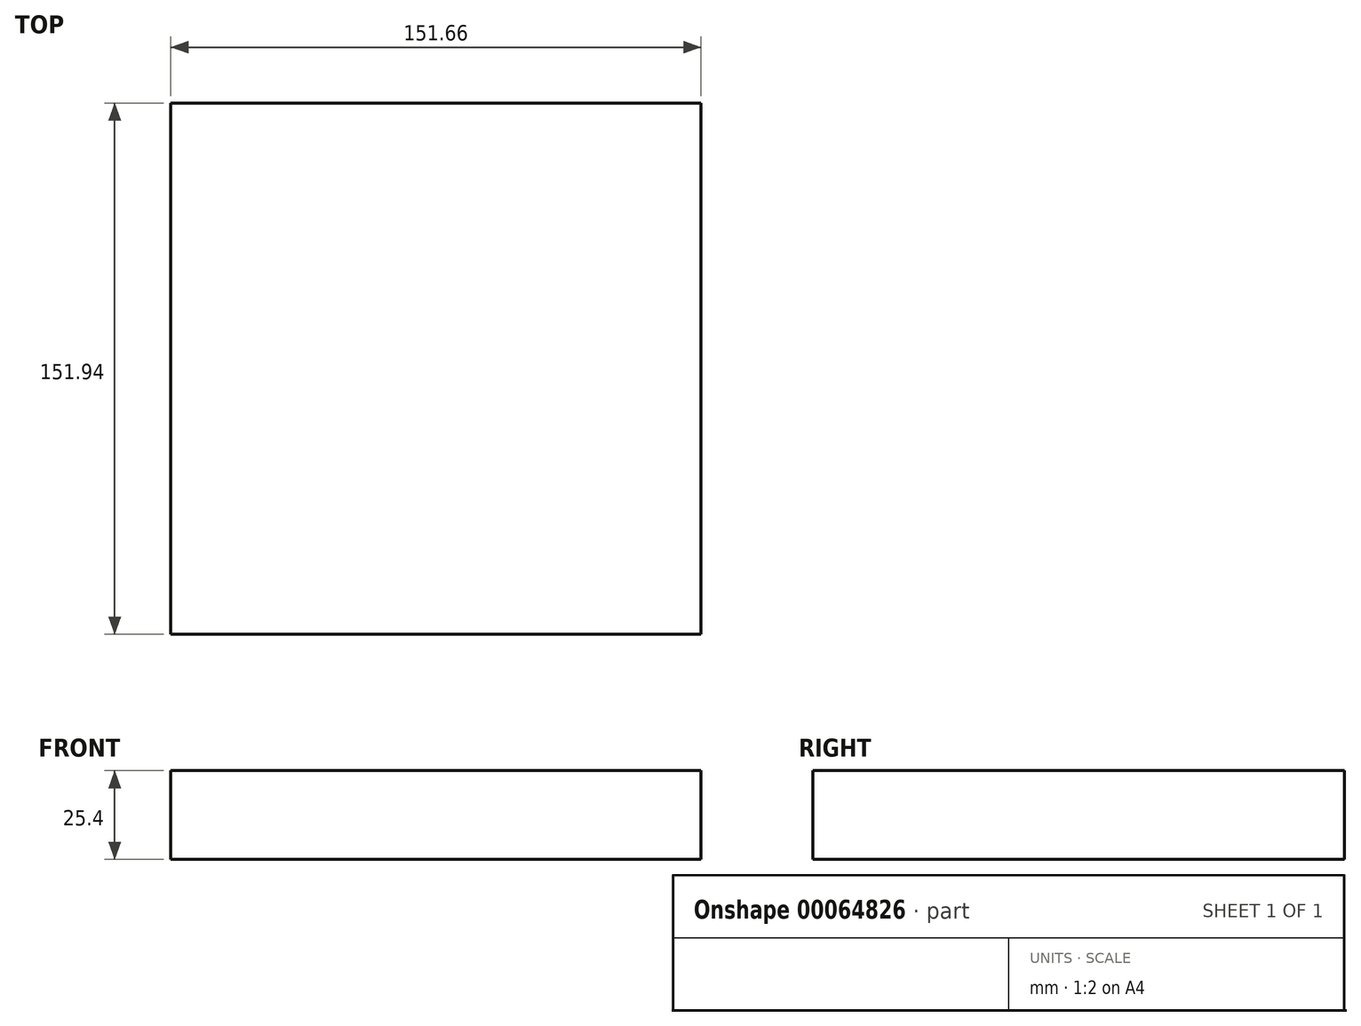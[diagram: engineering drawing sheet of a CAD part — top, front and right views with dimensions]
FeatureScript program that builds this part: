
annotation { "Feature Type Name" : "Feature", "Feature Type Description" : "" }
export const myFeature = defineFeature(function(context is Context, id is Id, definition is map)
    precondition{}
    {
        {
            var Q0;
            Q0=qCreatedBy(makeId("Top.planeOp"),FACE);
            var sketch = newSketch(context, id + "F0", { "sketchPlane" : qUnion([Q0])});
            skLineSegment(sketch, "E0.bottom", {"start": v(-75.74, -76.22) * mm, "end": v(75.92, -76.22) * mm});
            skLineSegment(sketch, "E0.top", {"start": v(-75.74, 75.72) * mm, "end": v(75.92, 75.72) * mm});
            skLineSegment(sketch, "E0.left", {"start": v(-75.74, -76.22) * mm, "end": v(-75.74, 75.72) * mm});
            skLineSegment(sketch, "E0.right", {"start": v(75.92, -76.22) * mm, "end": v(75.92, 75.72) * mm});
            skSolve(sketch);
        }
        {
            var Q0;
            Q0=makeQuery(id+"F0.imprint","IMPRINT",FACE,{"disambiguationData":[TD([[makeQuery(id+"F0.imprint","IMPRINT",EDGE,{"derivedFrom":sQuery(id+"F0.wireOp",EDGE,"E0.bottom")}),1.0]])]});
            extrude(context, id + "F1", {"entities" : qUnion([Q0]), "depth" : 25.4 * mm});
        }
    });
